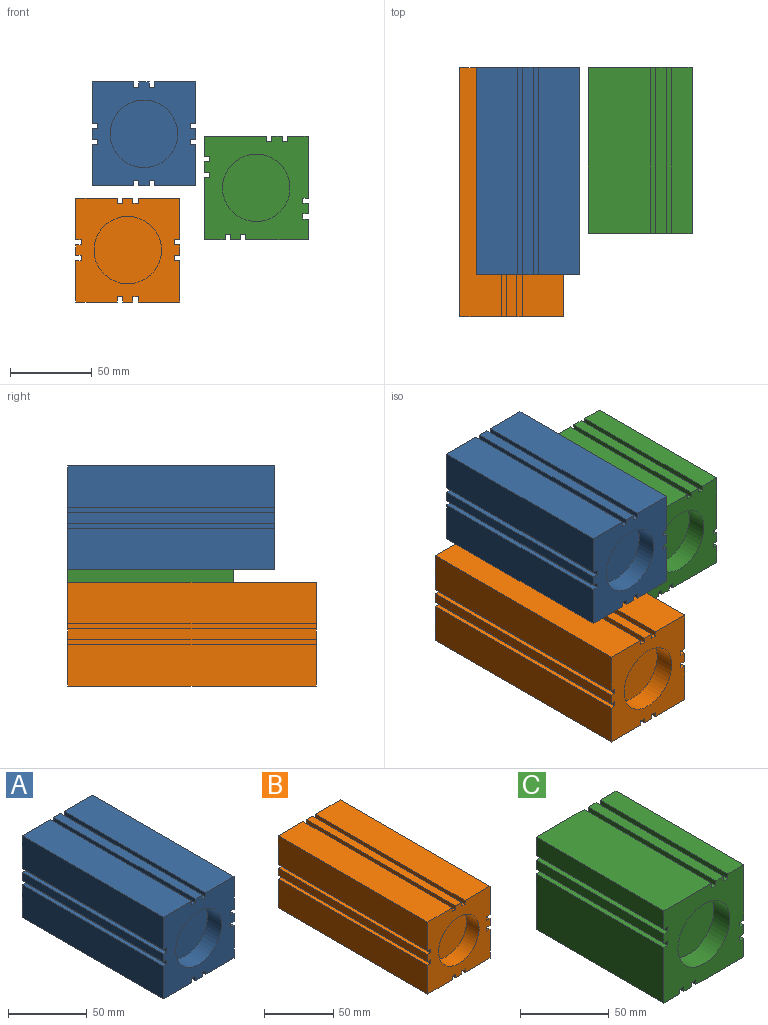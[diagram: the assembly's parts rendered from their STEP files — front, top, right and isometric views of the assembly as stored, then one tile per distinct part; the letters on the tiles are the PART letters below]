
ASSEMBLY  parts=3 mates=2
PART A: 40 faces, bbox 63.5x127x63.5 mm
  f0: plane 127x25.4mm, normal (0,0,-1), area 3225.8mm2, adj f2,f4,f13,f37
  f1: plane 127x6.35mm, normal (0,0,-1), area 806.4mm2, adj f2,f13,f34,f38
  f2: plane 63.5x63.5mm, normal (0,-1,0), area 2613.6mm2, adj f0,f1,f3,f4,f5,f6,f7,f8
  f3: plane 127x6.35mm, normal (-1,0,0), area 806.4mm2, adj f2,f13,f28,f32
  f4: plane 127x25.4mm, normal (-1,0,0), area 3225.8mm2, adj f0,f2,f13,f29
  f5: plane 127x25.4mm, normal (0,0,1), area 3225.8mm2, adj f2,f9,f13,f26
  f6: plane 127x6.35mm, normal (0,0,1), area 806.4mm2, adj f2,f13,f23,f25
  f7: plane 127x25.4mm, normal (1,0,0), area 3225.8mm2, adj f2,f10,f13,f19
  f8: plane 127x6.35mm, normal (1,0,0), area 806.4mm2, adj f2,f13,f17,f20
  f9: plane 127x25.4mm, normal (-1,0,0), area 3225.8mm2, adj f2,f5,f13,f31
  f10: plane 127x25.4mm, normal (0,0,-1), area 3225.8mm2, adj f2,f7,f13,f35
  f11: plane 127x25.4mm, normal (1,0,0), area 3225.8mm2, adj f2,f12,f13,f16
  f12: plane 127x25.4mm, normal (0,0,1), area 3225.8mm2, adj f2,f11,f13,f22
  f13: plane 63.5x63.5mm, normal (0,1,0), area 3951.6mm2, adj f0,f1,f3,f4,f5,f6,f7,f8
  f14: cylinder r=20.64mm len=41.28mm, axis (0,-1,0), area 1646.8mm2, adj f2,f15
  f15: plane 41.28x41.28mm, normal (0,-1,0), area 1338mm2, adj f14
  f16: plane 127x3.18mm, normal (0,0,-1), area 403.2mm2, adj f2,f11,f13,f18
  f17: plane 127x3.18mm, normal (0,0,1), area 403.2mm2, adj f2,f8,f13,f18
  f18: plane 127x3.18mm, normal (1,0,0), area 403.2mm2, adj f2,f13,f16,f17
  f19: plane 127x3.18mm, normal (0,0,1), area 403.2mm2, adj f2,f7,f13,f21
  f20: plane 127x3.18mm, normal (0,0,-1), area 403.2mm2, adj f2,f8,f13,f21
  f21: plane 127x3.18mm, normal (1,0,0), area 403.2mm2, adj f2,f13,f19,f20
  f22: plane 127x3.18mm, normal (-1,0,0), area 403.2mm2, adj f2,f12,f13,f24
  f23: plane 127x3.18mm, normal (1,0,0), area 403.2mm2, adj f2,f6,f13,f24
  f24: plane 127x3.18mm, normal (0,0,1), area 403.2mm2, adj f2,f13,f22,f23
  f25: plane 127x3.18mm, normal (-1,0,0), area 403.2mm2, adj f2,f6,f13,f27
  f26: plane 127x3.18mm, normal (1,0,0), area 403.2mm2, adj f2,f5,f13,f27
  f27: plane 127x3.18mm, normal (0,0,1), area 403.2mm2, adj f2,f13,f25,f26
  f28: plane 127x3.18mm, normal (0,0,-1), area 403.2mm2, adj f2,f3,f13,f30
  f29: plane 127x3.18mm, normal (0,0,1), area 403.2mm2, adj f2,f4,f13,f30
  f30: plane 127x3.18mm, normal (-1,0,0), area 403.2mm2, adj f2,f13,f28,f29
  f31: plane 127x3.18mm, normal (0,0,-1), area 403.2mm2, adj f2,f9,f13,f33
  f32: plane 127x3.18mm, normal (0,0,1), area 403.2mm2, adj f2,f3,f13,f33
  f33: plane 127x3.18mm, normal (-1,0,0), area 403.2mm2, adj f2,f13,f31,f32
  f34: plane 127x3.18mm, normal (1,0,0), area 403.2mm2, adj f1,f2,f13,f36
  f35: plane 127x3.18mm, normal (-1,0,0), area 403.2mm2, adj f2,f10,f13,f36
  f36: plane 127x3.18mm, normal (0,0,-1), area 403.2mm2, adj f2,f13,f34,f35
  f37: plane 127x3.18mm, normal (1,0,0), area 403.2mm2, adj f0,f2,f13,f39
  f38: plane 127x3.18mm, normal (-1,0,0), area 403.2mm2, adj f1,f2,f13,f39
  f39: plane 127x3.18mm, normal (0,0,-1), area 403.2mm2, adj f2,f13,f37,f38
PART B: 40 faces, bbox 63.5x152.4x63.5 mm
  f0: plane 152.4x25.4mm, normal (0,0,-1), area 3871mm2, adj f2,f4,f13,f37
  f1: plane 152.4x6.35mm, normal (0,0,-1), area 967.7mm2, adj f2,f13,f34,f38
  f2: plane 63.5x63.5mm, normal (0,-1,0), area 2613.6mm2, adj f0,f1,f3,f4,f5,f6,f7,f8
  f3: plane 152.4x6.35mm, normal (-1,0,0), area 967.7mm2, adj f2,f13,f28,f32
  f4: plane 152.4x25.4mm, normal (-1,0,0), area 3871mm2, adj f0,f2,f13,f29
  f5: plane 152.4x25.4mm, normal (0,0,1), area 3871mm2, adj f2,f9,f13,f26
  f6: plane 152.4x6.35mm, normal (0,0,1), area 967.7mm2, adj f2,f13,f23,f25
  f7: plane 152.4x25.4mm, normal (1,0,0), area 3871mm2, adj f2,f10,f13,f19
  f8: plane 152.4x6.35mm, normal (1,0,0), area 967.7mm2, adj f2,f13,f17,f20
  f9: plane 152.4x25.4mm, normal (-1,0,0), area 3871mm2, adj f2,f5,f13,f31
  f10: plane 152.4x25.4mm, normal (0,0,-1), area 3871mm2, adj f2,f7,f13,f35
  f11: plane 152.4x25.4mm, normal (1,0,0), area 3871mm2, adj f2,f12,f13,f16
  f12: plane 152.4x25.4mm, normal (0,0,1), area 3871mm2, adj f2,f11,f13,f22
  f13: plane 63.5x63.5mm, normal (0,1,0), area 3951.6mm2, adj f0,f1,f3,f4,f5,f6,f7,f8
  f14: cylinder r=20.64mm len=41.28mm, axis (0,-1,0), area 1646.8mm2, adj f2,f15
  f15: plane 41.28x41.28mm, normal (0,-1,0), area 1338mm2, adj f14
  f16: plane 152.4x3.18mm, normal (0,0,-1), area 483.9mm2, adj f2,f11,f13,f18
  f17: plane 152.4x3.18mm, normal (0,0,1), area 483.9mm2, adj f2,f8,f13,f18
  f18: plane 152.4x3.18mm, normal (1,0,0), area 483.9mm2, adj f2,f13,f16,f17
  f19: plane 152.4x3.18mm, normal (0,0,1), area 483.9mm2, adj f2,f7,f13,f21
  f20: plane 152.4x3.18mm, normal (0,0,-1), area 483.9mm2, adj f2,f8,f13,f21
  f21: plane 152.4x3.18mm, normal (1,0,0), area 483.9mm2, adj f2,f13,f19,f20
  f22: plane 152.4x3.18mm, normal (-1,0,0), area 483.9mm2, adj f2,f12,f13,f24
  f23: plane 152.4x3.18mm, normal (1,0,0), area 483.9mm2, adj f2,f6,f13,f24
  f24: plane 152.4x3.18mm, normal (0,0,1), area 483.9mm2, adj f2,f13,f22,f23
  f25: plane 152.4x3.18mm, normal (-1,0,0), area 483.9mm2, adj f2,f6,f13,f27
  f26: plane 152.4x3.18mm, normal (1,0,0), area 483.9mm2, adj f2,f5,f13,f27
  f27: plane 152.4x3.18mm, normal (0,0,1), area 483.9mm2, adj f2,f13,f25,f26
  f28: plane 152.4x3.18mm, normal (0,0,-1), area 483.9mm2, adj f2,f3,f13,f30
  f29: plane 152.4x3.18mm, normal (0,0,1), area 483.9mm2, adj f2,f4,f13,f30
  f30: plane 152.4x3.18mm, normal (-1,0,0), area 483.9mm2, adj f2,f13,f28,f29
  f31: plane 152.4x3.18mm, normal (0,0,-1), area 483.9mm2, adj f2,f9,f13,f33
  f32: plane 152.4x3.18mm, normal (0,0,1), area 483.9mm2, adj f2,f3,f13,f33
  f33: plane 152.4x3.18mm, normal (-1,0,0), area 483.9mm2, adj f2,f13,f31,f32
  f34: plane 152.4x3.18mm, normal (1,0,0), area 483.9mm2, adj f1,f2,f13,f36
  f35: plane 152.4x3.18mm, normal (-1,0,0), area 483.9mm2, adj f2,f10,f13,f36
  f36: plane 152.4x3.18mm, normal (0,0,-1), area 483.9mm2, adj f2,f13,f34,f35
  f37: plane 152.4x3.18mm, normal (1,0,0), area 483.9mm2, adj f0,f2,f13,f39
  f38: plane 152.4x3.18mm, normal (-1,0,0), area 483.9mm2, adj f1,f2,f13,f39
  f39: plane 152.4x3.18mm, normal (0,0,-1), area 483.9mm2, adj f2,f13,f37,f38
PART C: 40 faces, bbox 63.5x101.6x63.5 mm
  f0: plane 101.6x12.7mm, normal (0,0,-1), area 1290.3mm2, adj f2,f4,f13,f37
  f1: plane 101.6x6.35mm, normal (0,0,-1), area 645.2mm2, adj f2,f13,f34,f38
  f2: plane 63.5x63.5mm, normal (0,-1,0), area 2613.6mm2, adj f0,f1,f3,f4,f5,f6,f7,f8
  f3: plane 101.6x6.35mm, normal (-1,0,0), area 645.2mm2, adj f2,f13,f28,f32
  f4: plane 101.6x38.1mm, normal (-1,0,0), area 3871mm2, adj f0,f2,f13,f29
  f5: plane 101.6x38.1mm, normal (0,0,1), area 3871mm2, adj f2,f9,f13,f26
  f6: plane 101.6x6.35mm, normal (0,0,1), area 645.2mm2, adj f2,f13,f23,f25
  f7: plane 101.6x12.7mm, normal (1,0,0), area 1290.3mm2, adj f2,f10,f13,f19
  f8: plane 101.6x6.35mm, normal (1,0,0), area 645.2mm2, adj f2,f13,f17,f20
  f9: plane 101.6x12.7mm, normal (-1,0,0), area 1290.3mm2, adj f2,f5,f13,f31
  f10: plane 101.6x38.1mm, normal (0,0,-1), area 3871mm2, adj f2,f7,f13,f35
  f11: plane 101.6x38.1mm, normal (1,0,0), area 3871mm2, adj f2,f12,f13,f16
  f12: plane 101.6x12.7mm, normal (0,0,1), area 1290.3mm2, adj f2,f11,f13,f22
  f13: plane 63.5x63.5mm, normal (0,1,0), area 3951.6mm2, adj f0,f1,f3,f4,f5,f6,f7,f8
  f14: cylinder r=20.64mm len=41.28mm, axis (0,-1,0), area 1646.8mm2, adj f2,f15
  f15: plane 41.28x41.28mm, normal (0,-1,0), area 1338mm2, adj f14
  f16: plane 101.6x3.18mm, normal (0,0,-1), area 322.6mm2, adj f2,f11,f13,f18
  f17: plane 101.6x3.18mm, normal (0,0,1), area 322.6mm2, adj f2,f8,f13,f18
  f18: plane 101.6x3.18mm, normal (1,0,0), area 322.6mm2, adj f2,f13,f16,f17
  f19: plane 101.6x3.18mm, normal (0,0,1), area 322.6mm2, adj f2,f7,f13,f21
  f20: plane 101.6x3.18mm, normal (0,0,-1), area 322.6mm2, adj f2,f8,f13,f21
  f21: plane 101.6x3.18mm, normal (1,0,0), area 322.6mm2, adj f2,f13,f19,f20
  f22: plane 101.6x3.18mm, normal (-1,0,0), area 322.6mm2, adj f2,f12,f13,f24
  f23: plane 101.6x3.18mm, normal (1,0,0), area 322.6mm2, adj f2,f6,f13,f24
  f24: plane 101.6x3.18mm, normal (0,0,1), area 322.6mm2, adj f2,f13,f22,f23
  f25: plane 101.6x3.18mm, normal (-1,0,0), area 322.6mm2, adj f2,f6,f13,f27
  f26: plane 101.6x3.18mm, normal (1,0,0), area 322.6mm2, adj f2,f5,f13,f27
  f27: plane 101.6x3.18mm, normal (0,0,1), area 322.6mm2, adj f2,f13,f25,f26
  f28: plane 101.6x3.18mm, normal (0,0,-1), area 322.6mm2, adj f2,f3,f13,f30
  f29: plane 101.6x3.18mm, normal (0,0,1), area 322.6mm2, adj f2,f4,f13,f30
  f30: plane 101.6x3.18mm, normal (-1,0,0), area 322.6mm2, adj f2,f13,f28,f29
  f31: plane 101.6x3.18mm, normal (0,0,-1), area 322.6mm2, adj f2,f9,f13,f33
  f32: plane 101.6x3.18mm, normal (0,0,1), area 322.6mm2, adj f2,f3,f13,f33
  f33: plane 101.6x3.18mm, normal (-1,0,0), area 322.6mm2, adj f2,f13,f31,f32
  f34: plane 101.6x3.18mm, normal (1,0,0), area 322.6mm2, adj f1,f2,f13,f36
  f35: plane 101.6x3.18mm, normal (-1,0,0), area 322.6mm2, adj f2,f10,f13,f36
  f36: plane 101.6x3.18mm, normal (0,0,-1), area 322.6mm2, adj f2,f13,f34,f35
  f37: plane 101.6x3.18mm, normal (1,0,0), area 322.6mm2, adj f0,f2,f13,f39
  f38: plane 101.6x3.18mm, normal (-1,0,0), area 322.6mm2, adj f1,f2,f13,f39
  f39: plane 101.6x3.18mm, normal (0,0,-1), area 322.6mm2, adj f2,f13,f37,f38
PLACE A t=(89.37,66.97,1.36)mm
PLACE B t=(79.48,66.97,-69.81)mm
PLACE C t=(158.12,66.97,-31.7)mm
MATE planar B.f14 <-> A.f14  axis (0,1,0) through (111.23,66.97,-38.06)mm
MATE planar A.f13 <-> C.f14  axis (0,1,0) through (149.7,66.97,39.46)mm
